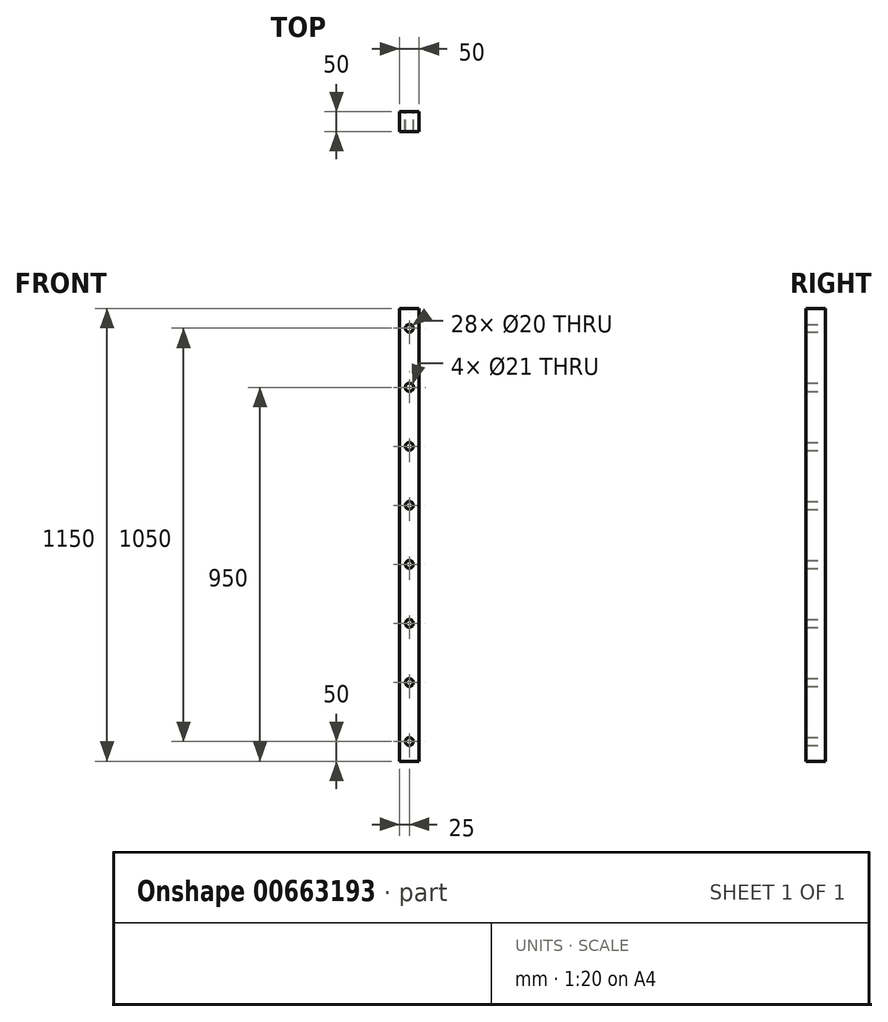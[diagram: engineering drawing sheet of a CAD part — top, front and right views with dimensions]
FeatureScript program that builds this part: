
annotation { "Feature Type Name" : "Feature", "Feature Type Description" : "" }
export const myFeature = defineFeature(function(context is Context, id is Id, definition is map)
    precondition{}
    {
        {
            var Q0;
            Q0=qCreatedBy(makeId("Top.planeOp"),FACE);
            var sketch = newSketch(context, id + "F0", { "sketchPlane" : qUnion([Q0])});
            skLineSegment(sketch, "E0.bottom", {"start": v(-25, 25) * mm, "end": v(25, 25) * mm});
            skLineSegment(sketch, "E0.top", {"start": v(-25, -25) * mm, "end": v(25, -25) * mm});
            skLineSegment(sketch, "E0.left", {"start": v(-25, 25) * mm, "end": v(-25, -25) * mm});
            skLineSegment(sketch, "E0.right", {"start": v(25, 25) * mm, "end": v(25, -25) * mm});
            skPoint(sketch, "E0.middle", {"position": v(0, 0) * mm});
            skSolve(sketch);
        }
        {
            var Q0;
            Q0=makeQuery(id+"F0.imprint","IMPRINT",FACE,{"disambiguationData":[TD([[makeQuery(id+"F0.imprint","IMPRINT",EDGE,{"derivedFrom":sQuery(id+"F0.wireOp",EDGE,"E0.bottom")}),-1.0]])]});
            extrude(context, id + "F1", {"entities" : qUnion([Q0]), "endBound" : BoundingType.SYMMETRIC, "depth" : 1150 * mm, "offsetDistance" : 25 * mm});
        }
        {
            var Q0;
            Q0=makeQuery(id+"F1.opExtrude","SWEPT_FACE",FACE,{"disambiguationData":[OSD([sQuery(id+"F0.wireOp",EDGE,"E0.bottom")])]});
            var sketch = newSketch(context, id + "F2", { "sketchPlane" : qUnion([Q0])});
            skCircle(sketch, "E1", {"center": v(0, 525) * mm, "radius": 10 * mm});
            skCircle(sketch, "E2", {"center": v(0, 375) * mm, "radius": 10.5 * mm});
            skLineSegment(sketch, "E3", {"start": v(0, 525) * mm, "end": v(10, 525) * mm});
            skLineSegment(sketch, "E4", {"start": v(0, 525) * mm, "end": v(0, -575) * mm});
            skCircle(sketch, "E5", {"center": v(0, 225) * mm, "radius": 10 * mm});
            skCircle(sketch, "E6", {"center": v(0, 75) * mm, "radius": 10 * mm});
            skCircle(sketch, "E7", {"center": v(0, -75) * mm, "radius": 10 * mm});
            skCircle(sketch, "E8", {"center": v(0, -225) * mm, "radius": 10 * mm});
            skCircle(sketch, "E9", {"center": v(0, -375) * mm, "radius": 10 * mm});
            skCircle(sketch, "E10", {"center": v(0, -525) * mm, "radius": 10 * mm});
            skCircle(sketch, "E11", {"center": v(0, -675) * mm, "radius": 10 * mm});
            skCircle(sketch, "E12", {"center": v(0, -825) * mm, "radius": 10 * mm});
            skCircle(sketch, "E13", {"center": v(0, -975) * mm, "radius": 10 * mm});
            skCircle(sketch, "E14", {"center": v(0, -1125) * mm, "radius": 10 * mm});
            skCircle(sketch, "E15", {"center": v(0, -1275) * mm, "radius": 10 * mm});
            skCircle(sketch, "E16", {"center": v(0, -1425) * mm, "radius": 10 * mm});
            skSolve(sketch);
        }
        {
            var Q0;
            Q0 = qSketchRegion(id + "F2", true);
            extrude(context, id + "F3", {"entities" : qUnion([Q0]), "operationType" : NewBodyOperationType.REMOVE, "oppositeDirection" : true, "depth" : 50 * mm, "offsetDistance" : 25 * mm});
        }
    });
